# Revit family: RSH_10_11_12_14_s150
name_source: partatom
category: Generic Models
units: mm (PartAtom-declared; Revit-internal decimal feet)

## family parameters
Always vertical = No
Can host rebar = Yes
Cut with Voids When Loaded = No
Part Type = Normal
Room Calculation Point = No
Round Connector Dimension = Use Diameter
Shared = No
Work Plane-Based = Yes

## types (8) — shared parameters
CenterToCenter = 150 mm
Default Elevation = 1219 mm

## per-type parameters (varying)
| type | Diameter Rebar | Length rebar | Model | Width Box | Width rebar |
| RSH 14 - 12 - 150mm | 12 mm  [stored 0.0393701 ft] | 610 mm | RSH 14_12_150 | 99 mm | 85 mm  [stored 0.278871 ft] |
| RSH 10 - 12 - 150mm | 12 mm  [stored 0.0393701 ft] | 610 mm | RSH_10_12_150 | 59 mm | 45 mm  [stored 0.147638 ft] |
| RSH 14 - 10 - 150mm | 10 mm  [stored 0.0328084 ft] | 540 mm | RSH 14_10_150 | 99 mm | 85 mm  [stored 0.278871 ft] |
| RSH 10 - 10 - 150mm | 10 mm  [stored 0.0328084 ft] | 540 mm | RSH_10_10_150 | 59 mm | 45 mm  [stored 0.147638 ft] |
| RSH 11 - 12 - 150mm | 12 mm  [stored 0.0393701 ft] | 610 mm | RSH_11_12_150 | 70 mm  [stored 0.229659 ft] | 55 mm  [stored 0.180446 ft] |
| RSH 11 - 10 - 150mm | 10 mm  [stored 0.0328084 ft] | 540 mm | RSH_11_10_150 | 70 mm  [stored 0.229659 ft] | 55 mm  [stored 0.180446 ft] |
| RSH 12 - 10 - 150mm | 10 mm  [stored 0.0328084 ft] | 540 mm | RSH_12_10_150 | 79 mm | 65 mm |
| RSH 12 - 12 - 150mm | 12 mm  [stored 0.0393701 ft] | 610 mm | RSH_12_10_150 | 79 mm | 65 mm |

note: [stored X ft] marks values corroborated as IEEE doubles in the binary element streams (Revit-internal decimal feet)

## geometry (parser evidence)
native form markers: Sweep x21
no freeform markers — native parametric forms only
